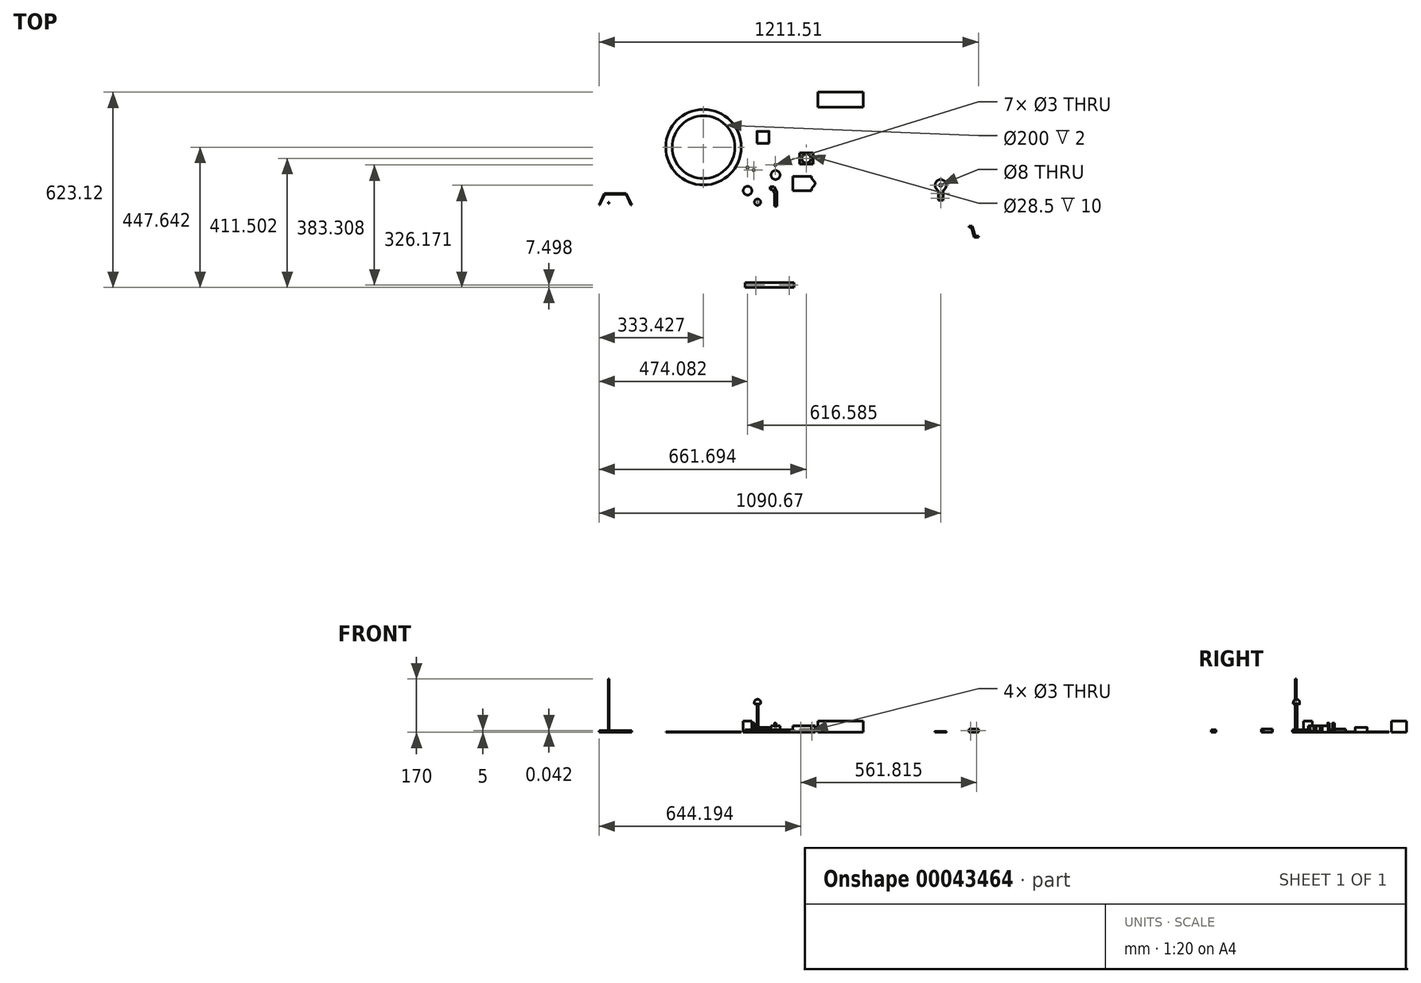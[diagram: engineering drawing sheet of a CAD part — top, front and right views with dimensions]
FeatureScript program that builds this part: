
annotation { "Feature Type Name" : "Feature", "Feature Type Description" : "" }
export const myFeature = defineFeature(function(context is Context, id is Id, definition is map)
    precondition{}
    {
        {
            var Q0;
            Q0=qCreatedBy(makeId("Top.planeOp"),FACE);
            var sketch = newSketch(context, id + "F0", { "sketchPlane" : qUnion([Q0])});
            skCircle(sketch, "E0", {"center": v(-57.73, 51.26) * mm, "radius": 2.75 * mm});
            skCircle(sketch, "E1", {"center": v(-57.73, 51.26) * mm, "radius": 1.5 * mm});
            skSolve(sketch);
        }
        {
            var Q0;
            Q0 = qSketchRegion(id + "F0", true);
            extrude(context, id + "F1", {"entities" : qUnion([Q0]), "depth" : 8 * mm});
        }
        {
            var Q0;
            Q0=qCreatedBy(makeId("Top.planeOp"),FACE);
            var sketch = newSketch(context, id + "F2", { "sketchPlane" : qUnion([Q0])});
            skCircle(sketch, "E2", {"center": v(-37.93, 42.72) * mm, "radius": 2.75 * mm});
            skCircle(sketch, "E3", {"center": v(-37.93, 42.72) * mm, "radius": 1.5 * mm});
            skSolve(sketch);
        }
        {
            var Q0;
            Q0 = qSketchRegion(id + "F2", true);
            extrude(context, id + "F3", {"entities" : qUnion([Q0]), "depth" : 30 * mm});
        }
        {
            var Q0;
            Q0=qCreatedBy(makeId("Top.planeOp"),FACE);
            var sketch = newSketch(context, id + "F4", { "sketchPlane" : qUnion([Q0])});
            skCircle(sketch, "E4", {"center": v(31.74, 27.18) * mm, "radius": 14.25 * mm});
            skSolve(sketch);
        }
        {
            var Q0;
            Q0 = qSketchRegion(id + "F4", true);
            extrude(context, id + "F5", {"entities" : qUnion([Q0]), "depth" : 20 * mm});
        }
        {
            var Q0;
            Q0=qCreatedBy(makeId("Top.planeOp"),FACE);
            var sketch = newSketch(context, id + "F6", { "sketchPlane" : qUnion([Q0])});
            skLineSegment(sketch, "E5", {"start": v(14.11, -10.68) * mm, "end": v(26.73, -10.68) * mm});
            skLineSegment(sketch, "E6", {"start": v(26.73, -10.68) * mm, "end": v(36.23, -27.14) * mm});
            skLineSegment(sketch, "E7", {"start": v(36.23, -27.14) * mm, "end": v(36.23, -72.14) * mm});
            skLineSegment(sketch, "E8", {"start": v(36.23, -72.14) * mm, "end": v(28.23, -72.14) * mm});
            skLineSegment(sketch, "E9", {"start": v(28.23, -72.14) * mm, "end": v(28.23, -29.28) * mm});
            skLineSegment(sketch, "E10", {"start": v(28.23, -29.28) * mm, "end": v(22.11, -18.68) * mm});
            skLineSegment(sketch, "E11", {"start": v(22.11, -18.68) * mm, "end": v(14.11, -18.68) * mm});
            skLineSegment(sketch, "E12", {"start": v(14.11, -18.68) * mm, "end": v(14.11, -10.68) * mm});
            skSolve(sketch);
        }
        {
            var Q0;
            Q0 = qSketchRegion(id + "F6", true);
            extrude(context, id + "F7", {"entities" : qUnion([Q0]), "depth" : 8 * mm});
        }
        {
            var Q0;
            Q0=qCreatedBy(makeId("Top.planeOp"),FACE);
            var sketch = newSketch(context, id + "F8", { "sketchPlane" : qUnion([Q0])});
            skCircle(sketch, "E13", {"center": v(-57.53, -23.01) * mm, "radius": 14 * mm});
            skSolve(sketch);
        }
        {
            var Q0;
            Q0 = qSketchRegion(id + "F8", true);
            extrude(context, id + "F9", {"entities" : qUnion([Q0]), "depth" : 36 * mm});
        }
        {
            var Q0;
            Q0=qCreatedBy(makeId("Top.planeOp"),FACE);
            var sketch = newSketch(context, id + "F10", { "sketchPlane" : qUnion([Q0])});
            skLineSegment(sketch, "E14", {"start": v(158.47, 0) * mm, "end": v(158.47, 3) * mm});
            skLineSegment(sketch, "E15", {"start": v(158.47, 3) * mm, "end": v(146.47, 16.5) * mm});
            skLineSegment(sketch, "E16", {"start": v(146.47, 16.5) * mm, "end": v(146.47, 22.5) * mm});
            skLineSegment(sketch, "E17", {"start": v(146.47, 22.5) * mm, "end": v(86.47, 22.5) * mm});
            skLineSegment(sketch, "E18", {"start": v(158.47, 0) * mm, "end": v(86.47, 0) * mm});
            skLineSegment(sketch, "E19", {"start": v(86.47, 0) * mm, "end": v(86.47, 22.5) * mm});
            skLineSegment(sketch, "E20.MirrorCS", {"start": v(146.47, -22.5) * mm, "end": v(86.47, -22.5) * mm});
            skLineSegment(sketch, "E21.MirrorCS", {"start": v(158.47, -3) * mm, "end": v(146.47, -16.5) * mm});
            skLineSegment(sketch, "E22.MirrorCS", {"start": v(146.47, -16.5) * mm, "end": v(146.47, -22.5) * mm});
            skLineSegment(sketch, "E23.MirrorCS", {"start": v(158.47, 0) * mm, "end": v(158.47, -3) * mm});
            skLineSegment(sketch, "E24.MirrorCS", {"start": v(86.47, 0) * mm, "end": v(86.47, -22.5) * mm});
            skSolve(sketch);
        }
        {
            var Q0;
            Q0 = qSketchRegion(id + "F10", true);
            extrude(context, id + "F11", {"entities" : qUnion([Q0]), "depth" : 20 * mm});
        }
        {
            var Q0;
            Q0=qCreatedBy(makeId("Top.planeOp"),FACE);
            var sketch = newSketch(context, id + "F12", { "sketchPlane" : qUnion([Q0])});
            skCircle(sketch, "E25", {"center": v(129.88, 79.74) * mm, "radius": 14.25 * mm});
            skLineSegment(sketch, "E26.bottom", {"start": v(108.38, 97.74) * mm, "end": v(151.38, 97.74) * mm});
            skLineSegment(sketch, "E26.top", {"start": v(108.38, 61.74) * mm, "end": v(151.38, 61.74) * mm});
            skLineSegment(sketch, "E26.left", {"start": v(108.38, 97.74) * mm, "end": v(108.38, 61.74) * mm});
            skLineSegment(sketch, "E26.right", {"start": v(151.38, 97.74) * mm, "end": v(151.38, 61.74) * mm});
            skSolve(sketch);
        }
        {
            var Q0;
            Q0 = qSketchRegion(id + "F12", true);
            extrude(context, id + "F13", {"entities" : qUnion([Q0]), "depth" : 10 * mm});
        }
        {
            var Q0;
            Q0=qCreatedBy(makeId("Top.planeOp"),FACE);
            var sketch = newSketch(context, id + "F14", { "sketchPlane" : qUnion([Q0])});
            skLineSegment(sketch, "E27.bottom", {"start": v(166.77, 243.36) * mm, "end": v(311.77, 243.36) * mm});
            skLineSegment(sketch, "E27.top", {"start": v(166.77, 291.36) * mm, "end": v(311.77, 291.36) * mm});
            skLineSegment(sketch, "E27.left", {"start": v(166.77, 243.36) * mm, "end": v(166.77, 291.36) * mm});
            skLineSegment(sketch, "E27.right", {"start": v(311.77, 243.36) * mm, "end": v(311.77, 291.36) * mm});
            skSolve(sketch);
        }
        {
            var Q0;
            Q0 = qSketchRegion(id + "F14", true);
            extrude(context, id + "F15", {"entities" : qUnion([Q0]), "depth" : 36 * mm});
        }
        {
            var Q0;
            Q0=qCreatedBy(makeId("Top.planeOp"),FACE);
            var sketch = newSketch(context, id + "F16", { "sketchPlane" : qUnion([Q0])});
            skCircle(sketch, "E28", {"center": v(-198.38, 115.88) * mm, "radius": 120.5 * mm});
            skCircle(sketch, "E29", {"center": v(-198.38, 115.88) * mm, "radius": 100 * mm});
            skSolve(sketch);
        }
        {
            var Q0;
            Q0 = qSketchRegion(id + "F16", true);
            extrude(context, id + "F17", {"entities" : qUnion([Q0]), "depth" : 2 * mm});
        }
        {
            var Q0;
            Q0=qCreatedBy(makeId("Top.planeOp"),FACE);
            var sketch = newSketch(context, id + "F18", { "sketchPlane" : qUnion([Q0])});
            skLineSegment(sketch, "E30.bottom", {"start": v(-65.28, -316.76) * mm, "end": v(90.22, -316.76) * mm});
            skLineSegment(sketch, "E30.top", {"start": v(-65.28, -331.76) * mm, "end": v(90.22, -331.76) * mm});
            skLineSegment(sketch, "E30.left", {"start": v(-65.28, -316.76) * mm, "end": v(-65.28, -331.76) * mm});
            skLineSegment(sketch, "E30.right", {"start": v(90.22, -316.76) * mm, "end": v(90.22, -331.76) * mm});
            skCircle(sketch, "E31", {"center": v(-31.28, -324.26) * mm, "radius": 1.5 * mm});
            skCircle(sketch, "E32", {"center": v(75.52, -324.26) * mm, "radius": 1.5 * mm});
            skSolve(sketch);
        }
        {
            var Q0;
            Q0 = qSketchRegion(id + "F18", true);
            extrude(context, id + "F19", {"entities" : qUnion([Q0]), "depth" : 8 * mm});
        }
        {
            var Q0;
            Q0=qCreatedBy(makeId("Top.planeOp"),FACE);
            var sketch = newSketch(context, id + "F20", { "sketchPlane" : qUnion([Q0])});
            skCircle(sketch, "E33", {"center": v(31.27, 59.05) * mm, "radius": 2.75 * mm});
            skCircle(sketch, "E34", {"center": v(31.27, 59.05) * mm, "radius": 1.5 * mm});
            skSolve(sketch);
        }
        {
            var Q0;
            Q0 = qSketchRegion(id + "F20", true);
            extrude(context, id + "F21", {"entities" : qUnion([Q0]), "depth" : 30 * mm});
        }
        {
            var Q0;
            Q0=qCreatedBy(makeId("Top.planeOp"),FACE);
            var sketch = newSketch(context, id + "F22", { "sketchPlane" : qUnion([Q0])});
            skLineSegment(sketch, "E35.bottom", {"start": v(-27.94, 166.6) * mm, "end": v(11.06, 166.6) * mm});
            skLineSegment(sketch, "E35.top", {"start": v(-27.94, 127.6) * mm, "end": v(11.06, 127.6) * mm});
            skLineSegment(sketch, "E35.left", {"start": v(-27.94, 166.6) * mm, "end": v(-27.94, 127.6) * mm});
            skLineSegment(sketch, "E35.right", {"start": v(11.06, 166.6) * mm, "end": v(11.06, 127.6) * mm});
            skSolve(sketch);
        }
        {
            var Q0;
            Q0 = qSketchRegion(id + "F22", true);
            extrude(context, id + "F23", {"entities" : qUnion([Q0]), "depth" : 15 * mm});
        }
        {
            var Q0;
            Q0=makeQuery(id+"F23.opExtrude","CAP_FACE",FACE,{"disambiguationData":[OSD([sQuery(id+"F22.wireOp",EDGE,"E35.bottom"),sQuery(id+"F22.wireOp",EDGE,"E35.top"),sQuery(id+"F22.wireOp",EDGE,"E35.left"),sQuery(id+"F22.wireOp",EDGE,"E35.right")])],"isStart":false});
            fillet(context, id + "F24", {"entities" : qUnion([Q0]), "radius" : 1 * mm, "tangentPropagation" : true, "allowEdgeOverflow" : false});
        }
        {
            var Q0;
            Q0=qCreatedBy(makeId("Top.planeOp"),FACE);
            var sketch = newSketch(context, id + "F25", { "sketchPlane" : qUnion([Q0])});
            skLineSegment(sketch, "E36.bottom", {"start": v(-502.88, -60.44) * mm, "end": v(-499.88, -60.44) * mm});
            skLineSegment(sketch, "E36.top", {"start": v(-502.88, -63.44) * mm, "end": v(-499.88, -63.44) * mm});
            skLineSegment(sketch, "E36.left", {"start": v(-502.88, -60.44) * mm, "end": v(-502.88, -63.44) * mm});
            skLineSegment(sketch, "E36.right", {"start": v(-499.88, -60.44) * mm, "end": v(-499.88, -63.44) * mm});
            skSolve(sketch);
        }
        {
            var Q0;
            Q0 = qSketchRegion(id + "F25", true);
            extrude(context, id + "F26", {"entities" : qUnion([Q0]), "depth" : 170 * mm});
        }
        {
            var Q0;
            Q0=qCreatedBy(makeId("Top.planeOp"),FACE);
            var sketch = newSketch(context, id + "F27", { "sketchPlane" : qUnion([Q0])});
            skLineSegment(sketch, "E37", {"start": v(-531.8, -69.24) * mm, "end": v(-514.7, -32.24) * mm});
            skLineSegment(sketch, "E38", {"start": v(-514.7, -32.24) * mm, "end": v(-445.13, -32.24) * mm});
            skLineSegment(sketch, "E39", {"start": v(-445.13, -32.24) * mm, "end": v(-427.8, -69.24) * mm});
            skLineSegment(sketch, "E40", {"start": v(-531.8, -69.24) * mm, "end": v(-530.16, -69.24) * mm});
            skLineSegment(sketch, "E41", {"start": v(-530.16, -69.24) * mm, "end": v(-513.98, -34.24) * mm});
            skLineSegment(sketch, "E42", {"start": v(-513.98, -34.24) * mm, "end": v(-445.85, -34.24) * mm});
            skLineSegment(sketch, "E43", {"start": v(-445.85, -34.24) * mm, "end": v(-429.46, -69.24) * mm});
            skLineSegment(sketch, "E44", {"start": v(-429.46, -69.24) * mm, "end": v(-427.8, -69.24) * mm});
            skSolve(sketch);
        }
        {
            var Q0;
            Q0 = qSketchRegion(id + "F27", true);
            extrude(context, id + "F28", {"entities" : qUnion([Q0]), "depth" : 5 * mm});
        }
        {
            var Q0;
            Q0=qCreatedBy(makeId("Top.planeOp"),FACE);
            var sketch = newSketch(context, id + "F29", { "sketchPlane" : qUnion([Q0])});
            skCircle(sketch, "E45", {"center": v(-25.78, -59.53) * mm, "radius": 2 * mm});
            skSolve(sketch);
        }
        {
            var Q0;
            Q0 = qSketchRegion(id + "F29", true);
            extrude(context, id + "F30", {"entities" : qUnion([Q0]), "depth" : 90 * mm});
        }
        {
            var Q0;
            Q0=makeQuery(id+"F30.opExtrude","CAP_FACE",FACE,{"disambiguationData":[OSD([sQuery(id+"F29.wireOp",EDGE,"E45")])],"isStart":false});
            var sketch = newSketch(context, id + "F31", { "sketchPlane" : qUnion([Q0])});
            skCircle(sketch, "E46", {"center": v(-25.78, -59.53) * mm, "radius": 10 * mm});
            skSolve(sketch);
        }
        {
            var Q0;
            Q0 = qSketchRegion(id + "F31", true);
            extrude(context, id + "F32", {"entities" : qUnion([Q0]), "operationType" : NewBodyOperationType.ADD, "depth" : 15 * mm});
        }
        {
            var Q0;
            Q0=makeQuery(id+"F32.opExtrude","CAP_EDGE",EDGE,{"disambiguationData":[OSD([sQuery(id+"F31.wireOp",EDGE,"E46")])],"isStart":false});
            fillet(context, id + "F33", {"entities" : qUnion([Q0]), "radius" : 9 * mm, "tangentPropagation" : true, "allowEdgeOverflow" : false});
        }
        {
            var Q0;
            Q0=qCreatedBy(makeId("Top.planeOp"),FACE);
            var sketch = newSketch(context, id + "F34", { "sketchPlane" : qUnion([Q0])});
            skLineSegment(sketch, "E47", {"start": v(679.7, -171.26) * mm, "end": v(679.7, -167.26) * mm});
            skLineSegment(sketch, "E48", {"start": v(679.7, -167.26) * mm, "end": v(668.2, -167.26) * mm});
            skLineSegment(sketch, "E49", {"start": v(659.7, -135.76) * mm, "end": v(649.7, -135.76) * mm});
            skLineSegment(sketch, "E50", {"start": v(649.7, -135.76) * mm, "end": v(649.7, -139.76) * mm});
            skLineSegment(sketch, "E51", {"start": v(649.7, -139.76) * mm, "end": v(656.67, -139.76) * mm});
            skLineSegment(sketch, "E52", {"start": v(665.6, -171.26) * mm, "end": v(679.7, -171.26) * mm});
            skLineSegment(sketch, "E53", {"start": v(668.2, -167.26) * mm, "end": v(668.2, -165.76) * mm});
            skLineSegment(sketch, "E54", {"start": v(668.2, -165.76) * mm, "end": v(659.7, -135.76) * mm});
            skLineSegment(sketch, "E55", {"start": v(656.67, -139.76) * mm, "end": v(665.6, -171.26) * mm});
            skSolve(sketch);
        }
        {
            var Q0;
            Q0 = qSketchRegion(id + "F34", true);
            extrude(context, id + "F35", {"entities" : qUnion([Q0]), "depth" : 10 * mm});
        }
        {
            var Q0;
            Q0=makeQuery(id+"F35.opExtrude","SWEPT_FACE",FACE,{"disambiguationData":[OSD([sQuery(id+"F34.wireOp",EDGE,"E49")])]});
            var sketch = newSketch(context, id + "F36", { "sketchPlane" : qUnion([Q0])});
            skCircle(sketch, "E56", {"center": v(-654.2, 5) * mm, "radius": 1.5 * mm});
            skCircle(sketch, "E57", {"center": v(-674.2, 5) * mm, "radius": 1.5 * mm});
            skSolve(sketch);
        }
        {
            var Q0;
            Q0 = qSketchRegion(id + "F36", true);
            extrude(context, id + "F37", {"entities" : qUnion([Q0]), "operationType" : NewBodyOperationType.REMOVE, "oppositeDirection" : true, "depth" : 40 * mm});
        }
        {
            var Q0;
            Q0=qCreatedBy(makeId("Top.planeOp"),FACE);
            var sketch = newSketch(context, id + "F38", { "sketchPlane" : qUnion([Q0])});
            skLineSegment(sketch, "E58.bottom", {"start": v(566.36, -23.59) * mm, "end": v(551.36, -23.59) * mm});
            skLineSegment(sketch, "E58.top", {"start": v(566.36, -53.59) * mm, "end": v(551.36, -53.59) * mm});
            skLineSegment(sketch, "E58.left", {"start": v(566.36, -23.59) * mm, "end": v(566.36, -53.59) * mm});
            skLineSegment(sketch, "E58.right", {"start": v(551.36, -23.59) * mm, "end": v(551.36, -53.59) * mm});
            skCircle(sketch, "E59", {"center": v(558.86, -5.59) * mm, "radius": 18 * mm});
            skPoint(sketch, "E60", {"position": v(558.86, -23.59) * mm});
            skCircle(sketch, "E61", {"center": v(543.86, -26.21) * mm, "radius": 7.5 * mm});
            skCircle(sketch, "E62", {"center": v(573.86, -26.21) * mm, "radius": 7.5 * mm});
            skCircle(sketch, "E63", {"center": v(558.86, -31.59) * mm, "radius": 1.5 * mm});
            skCircle(sketch, "E64", {"center": v(558.86, -47.59) * mm, "radius": 1.5 * mm});
            skCircle(sketch, "E65", {"center": v(558.86, -5.59) * mm, "radius": 4 * mm});
            skSolve(sketch);
        }
        {
            var Q0;
            {var subQ0=sQuery(id+"F38.wireOp",EDGE,"E58.left");var subQ1=sQuery(id+"F38.wireOp",EDGE,"E58.bottom");var subQ2=makeQuery(id+"F38.imprint","INTERSECT",VERTEX,{"derivedFrom":[subQ1,subQ0]});Q0=makeQuery(id+"F38.imprint","IMPRINT",FACE,{"disambiguationData":[TD([[makeQuery(id+"F38.imprint","IMPRINT",EDGE,{"disambiguationData":[TD([[subQ2,-1.0]])],"derivedFrom":subQ1}),-1.0]])]});}
            var Q1;
            {var subQ0=sQuery(id+"F38.wireOp",EDGE,"E58.right");var subQ1=sQuery(id+"F38.wireOp",EDGE,"E58.bottom");var subQ2=makeQuery(id+"F38.imprint","INTERSECT",VERTEX,{"derivedFrom":[subQ1,subQ0]});Q1=makeQuery(id+"F38.imprint","IMPRINT",FACE,{"disambiguationData":[TD([[makeQuery(id+"F38.imprint","IMPRINT",EDGE,{"disambiguationData":[TD([[subQ2,1.0]])],"derivedFrom":subQ1}),-1.0]])]});}
            var Q2;
            Q2=makeQuery(id+"F38.imprint","IMPRINT",FACE,{"disambiguationData":[TD([[makeQuery(id+"F38.imprint","IMPRINT",EDGE,{"derivedFrom":sQuery(id+"F38.wireOp",EDGE,"E65")}),-1.0]])]});
            var Q3;
            {var subQ4=sQuery(id+"F38.wireOp",EDGE,"E58.top");Q3=makeQuery(id+"F38.imprint","IMPRINT",FACE,{"disambiguationData":[TD([[makeQuery(id+"F38.imprint","IMPRINT",EDGE,{"derivedFrom":subQ4}),-1.0]])]});}
            extrude(context, id + "F39", {"entities" : qUnion([Q0, Q1, Q2, Q3]), "depth" : 3 * mm});
        }
        {
            var Q0;
            Q0=makeQuery(id+"F13.opExtrude","SWEPT_FACE",FACE,{"disambiguationData":[OSD([sQuery(id+"F12.wireOp",EDGE,"E26.bottom")])]});
            var sketch = newSketch(context, id + "F40", { "sketchPlane" : qUnion([Q0])});
            skCircle(sketch, "E66", {"center": v(-112.38, 5.04) * mm, "radius": 1.5 * mm});
            skCircle(sketch, "E67", {"center": v(-147.38, 5.04) * mm, "radius": 1.5 * mm});
            skSolve(sketch);
        }
        {
            var Q0;
            Q0 = qSketchRegion(id + "F40", true);
            extrude(context, id + "F41", {"entities" : qUnion([Q0]), "operationType" : NewBodyOperationType.REMOVE, "oppositeDirection" : true, "depth" : 45 * mm});
        }
    });
